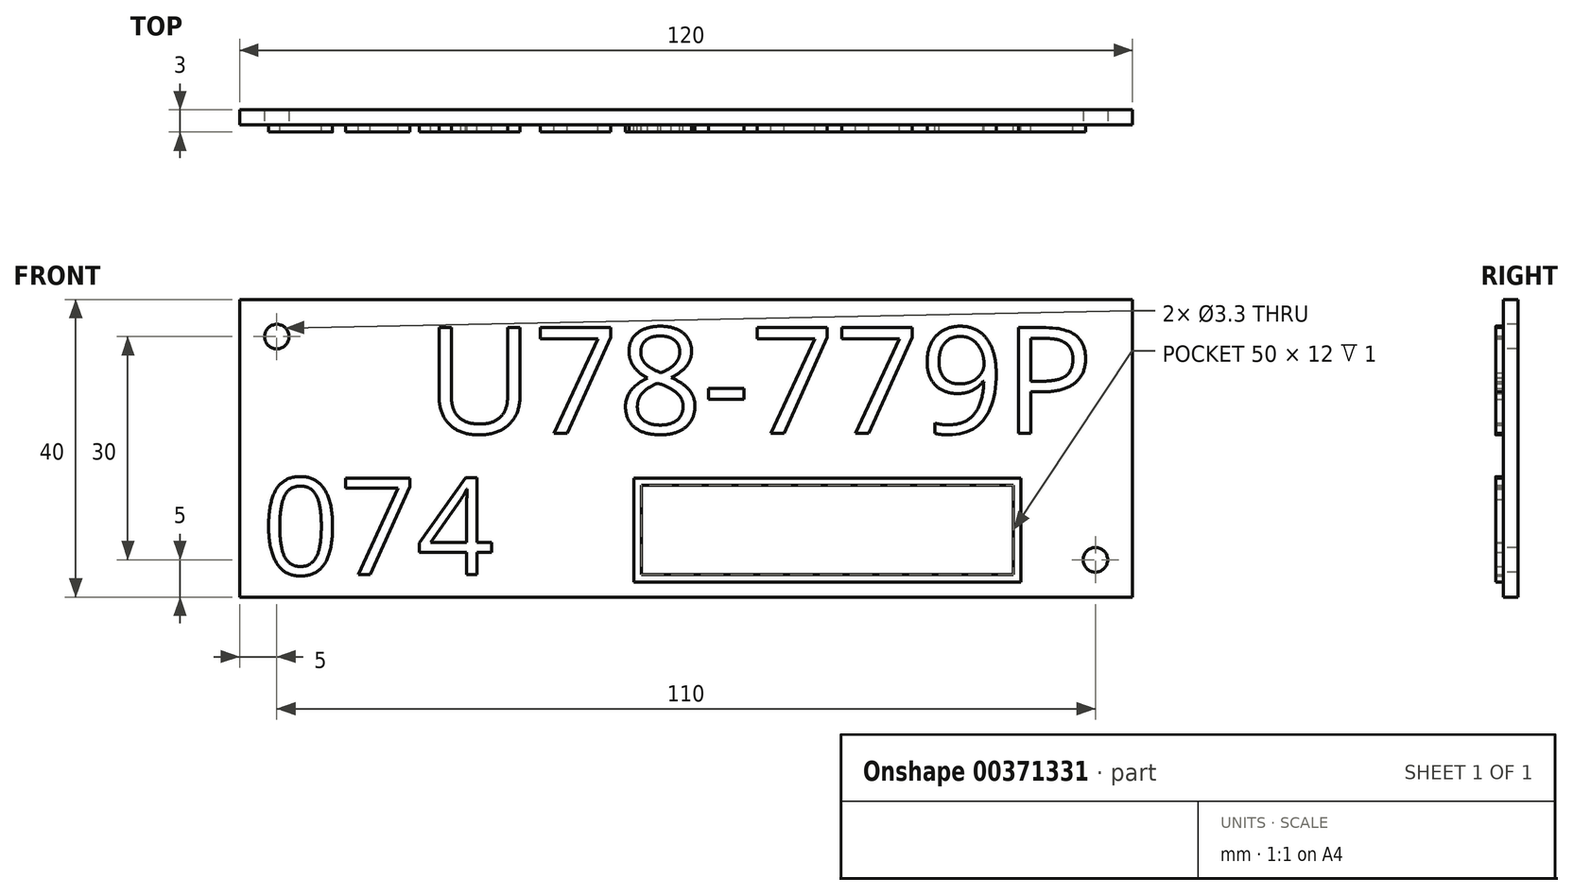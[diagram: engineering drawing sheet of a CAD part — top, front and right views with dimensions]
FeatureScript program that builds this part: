
annotation { "Feature Type Name" : "Feature", "Feature Type Description" : "" }
export const myFeature = defineFeature(function(context is Context, id is Id, definition is map)
    precondition{}
    {
        {
            var Q0;
            Q0=qCreatedBy(makeId("Front.planeOp"),FACE);
            var sketch = newSketch(context, id + "F0", { "sketchPlane" : qUnion([Q0])});
            skLineSegment(sketch, "E0.bottom", {"start": v(60, -20) * mm, "end": v(-60, -20) * mm});
            skLineSegment(sketch, "E0.top", {"start": v(60, 20) * mm, "end": v(-60, 20) * mm});
            skLineSegment(sketch, "E0.left", {"start": v(60, -20) * mm, "end": v(60, 20) * mm});
            skLineSegment(sketch, "E0.right", {"start": v(-60, -20) * mm, "end": v(-60, 20) * mm});
            skPoint(sketch, "E0.middle", {"position": v(0, 0) * mm});
            skSolve(sketch);
        }
        {
            var Q0;
            Q0=makeQuery(id+"F0.imprint","IMPRINT",FACE,{"disambiguationData":[TD([[makeQuery(id+"F0.imprint","IMPRINT",EDGE,{"derivedFrom":sQuery(id+"F0.wireOp",EDGE,"E0.bottom")}),-1.0]])]});
            extrude(context, id + "F1", {"entities" : qUnion([Q0]), "depth" : 2 * mm});
        }
        {
            var Q0;
            Q0=makeQuery(id+"F1.opExtrude","CAP_FACE",FACE,{"disambiguationData":[OSD([sQuery(id+"F0.wireOp",EDGE,"E0.bottom"),sQuery(id+"F0.wireOp",EDGE,"E0.top"),sQuery(id+"F0.wireOp",EDGE,"E0.left"),sQuery(id+"F0.wireOp",EDGE,"E0.right")])],"isStart":false});
            var sketch = newSketch(context, id + "F2", { "sketchPlane" : qUnion([Q0])});
            skPoint(sketch, "E1", {"position": v(-55, 15) * mm});
            skPoint(sketch, "E2", {"position": v(55, -15) * mm});
            skSolve(sketch);
        }
        {
            var Q0;
            Q0=sQuery(id+"F2.wireOp",VERTEX,"E1");
            var Q1;
            Q1=sQuery(id+"F2.wireOp",VERTEX,"E2");
            var Q2;
            Q2=makeQuery(id+"F1.opExtrude","SWEPT_BODY",BODY,{"disambiguationData":[OSD([sQuery(id+"F0.wireOp",EDGE,"E0.bottom"),sQuery(id+"F0.wireOp",EDGE,"E0.top"),sQuery(id+"F0.wireOp",EDGE,"E0.left"),sQuery(id+"F0.wireOp",EDGE,"E0.right")])]});
            hole(context, id + "F3", {"style" : HoleStyle.SIMPLE, "endStyle" : HoleEndStyle.THROUGH, "holeDiameter" : 3.3 * mm, "locations" : qUnion([Q0, Q1]), "scope" : qUnion([Q2]), "isTappedThrough" : true});
        }
        {
            var Q0;
            Q0=makeQuery(id+"F1.opExtrude","CAP_FACE",FACE,{"disambiguationData":[OSD([sQuery(id+"F0.wireOp",EDGE,"E0.bottom"),sQuery(id+"F0.wireOp",EDGE,"E0.top"),sQuery(id+"F0.wireOp",EDGE,"E0.left"),sQuery(id+"F0.wireOp",EDGE,"E0.right")])],"isStart":false});
            var sketch = newSketch(context, id + "F4", { "sketchPlane" : qUnion([Q0])});
            skText(sketch, "E3", { "text": "U78-779P", "fontName": "OpenSans-Regular.ttf"});
            const initialGuessF4  = {"E3": [-0.035, 0.002, 1, 0, 0.01432]};
            skSetInitialGuess(sketch, initialGuessF4);
            skSolve(sketch);
        }
        {
            var Q0;
            Q0=qSketchRegion(id+"F4",true);
            extrude(context, id + "F5", {"entities" : qUnion([Q0]), "operationType" : NewBodyOperationType.ADD, "depth" : 1 * mm});
        }
        {
            var Q0;
            {var subQ0=sQuery(id+"F0.wireOp",EDGE,"E0.top");var subQ1=sQuery(id+"F0.wireOp",EDGE,"E0.left");var subQ2=sQuery(id+"F0.wireOp",EDGE,"E0.right");var subQ3=sQuery(id+"F0.wireOp",EDGE,"E0.bottom");Q0=makeQuery(id+"F5.boolean.opBoolean","SPLIT",FACE,{"disambiguationData":[TD([makeQuery(id+"F1.opExtrude","SWEPT_FACE",FACE,{"disambiguationData":[OSD([subQ3])]})])],"derivedFrom":makeQuery(id+"F1.opExtrude","CAP_FACE",FACE,{"disambiguationData":[OSD([subQ3,subQ0,subQ1,subQ2])],"isStart":false})});}
            var sketch = newSketch(context, id + "F6", { "sketchPlane" : qUnion([Q0])});
            skText(sketch, "E4", { "text": "074", "fontName": "OpenSans-Regular.ttf"});
            const initialGuessF6  = {"E4": [-0.057, -0.017, 1, 0, 0.0131]};
            skSetInitialGuess(sketch, initialGuessF6);
            skSolve(sketch);
        }
        {
            var Q0;
            Q0=qSketchRegion(id+"F6",true);
            extrude(context, id + "F7", {"entities" : qUnion([Q0]), "operationType" : NewBodyOperationType.ADD, "depth" : 1 * mm});
        }
        {
            var Q0;
            {var subQ46=sQuery(id+"F0.wireOp",EDGE,"E0.top");var subQ48=sQuery(id+"F0.wireOp",EDGE,"E0.left");var subQ66=sQuery(id+"F0.wireOp",EDGE,"E0.right");var subQ76=sQuery(id+"F0.wireOp",EDGE,"E0.bottom");var subQ77=makeQuery(id+"F1.opExtrude","SWEPT_FACE",FACE,{"disambiguationData":[OSD([subQ76])]});Q0=makeQuery(id+"F7.boolean.opBoolean","SPLIT",FACE,{"disambiguationData":[TD([subQ77])],"derivedFrom":makeQuery(id+"F5.boolean.opBoolean","SPLIT",FACE,{"disambiguationData":[TD([subQ77])],"derivedFrom":makeQuery(id+"F1.opExtrude","CAP_FACE",FACE,{"disambiguationData":[OSD([subQ76,subQ46,subQ48,subQ66])],"isStart":false})})});}
            var sketch = newSketch(context, id + "F8", { "sketchPlane" : qUnion([Q0])});
            skLineSegment(sketch, "E5.bottom", {"start": v(45, -18) * mm, "end": v(-7, -18) * mm});
            skLineSegment(sketch, "E5.top", {"start": v(45, -4) * mm, "end": v(-7, -4) * mm});
            skLineSegment(sketch, "E5.left", {"start": v(45, -18) * mm, "end": v(45, -4) * mm});
            skLineSegment(sketch, "E5.right", {"start": v(-7, -18) * mm, "end": v(-7, -4) * mm});
            skPoint(sketch, "E5.middle", {"position": v(19, -11) * mm});
            skLineSegment(sketch, "E6.0", {"start": v(44, -5) * mm, "end": v(-6, -5) * mm});
            skLineSegment(sketch, "E6.1", {"start": v(44, -17) * mm, "end": v(44, -5) * mm});
            skLineSegment(sketch, "E6.2", {"start": v(44, -17) * mm, "end": v(-6, -17) * mm});
            skLineSegment(sketch, "E6.3", {"start": v(-6, -17) * mm, "end": v(-6, -5) * mm});
            skSolve(sketch);
        }
        {
            var Q0;
            Q0=makeQuery(id+"F8.imprint","IMPRINT",FACE,{"disambiguationData":[TD([[makeQuery(id+"F8.imprint","IMPRINT",EDGE,{"derivedFrom":sQuery(id+"F8.wireOp",EDGE,"E5.bottom")}),-1.0]])]});
            extrude(context, id + "F9", {"entities" : qUnion([Q0]), "operationType" : NewBodyOperationType.ADD, "depth" : 1 * mm});
        }
    });
